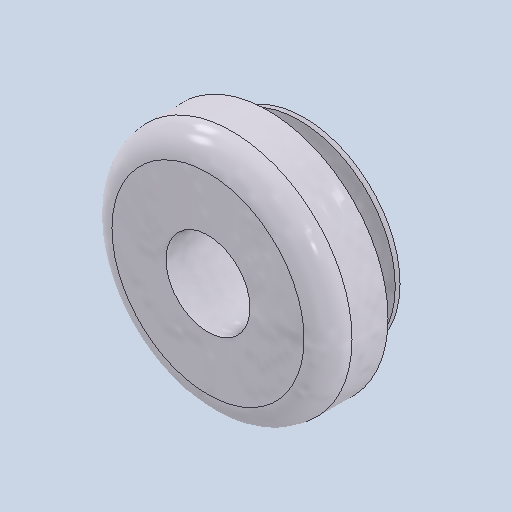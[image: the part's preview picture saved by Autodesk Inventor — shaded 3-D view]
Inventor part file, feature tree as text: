
AUTODESK INVENTOR PART (.ipt)
format: ipt  version: 2024.3 (Build 283343000, 343)  size: 155,136 bytes
history: native  units: in
note: dims shown in document units (in); Inventor stores cm internally (conversion verified against a paired STEP export)
features: other x3, sketch x2, plane x1
ambient origin geometry x8: Origin, YZ Plane, XZ Plane, XY Plane, X Axis, Y Axis, Z Axis, Center Point
bodies: Solid1 (feature_tree)
feature tree (6):
  other  "Pin.ipt"
  other  "Solid1::Pin.ipt"
  other  "TaggingFeature1"
  sketch  "Sketch1"  dims[d0=0.3937in]
  sketch  "Sketch2"
  plane  "Work Plane1"
